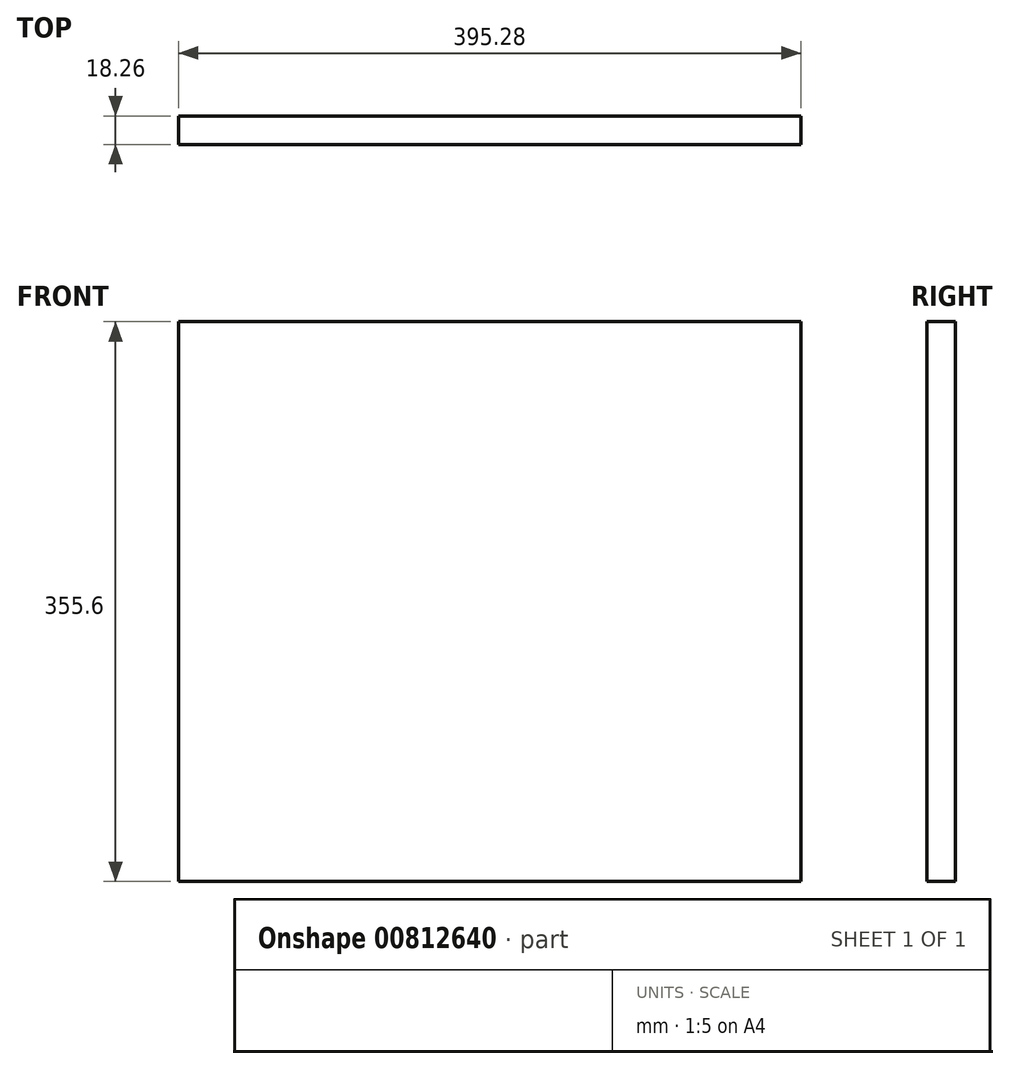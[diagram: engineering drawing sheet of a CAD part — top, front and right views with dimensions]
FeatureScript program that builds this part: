
annotation { "Feature Type Name" : "Feature", "Feature Type Description" : "" }
export const myFeature = defineFeature(function(context is Context, id is Id, definition is map)
    precondition{}
    {
        {
            var Q0;
            Q0=qCreatedBy(makeId("Front.planeOp"),FACE);
            var sketch = newSketch(context, id + "F0", { "sketchPlane" : qUnion([Q0])});
            skLineSegment(sketch, "E0.bottom", {"start": v(197.64, 177.8) * mm, "end": v(-197.64, 177.8) * mm});
            skLineSegment(sketch, "E0.top", {"start": v(197.64, -177.8) * mm, "end": v(-197.64, -177.8) * mm});
            skLineSegment(sketch, "E0.left", {"start": v(197.64, 177.8) * mm, "end": v(197.64, -177.8) * mm});
            skLineSegment(sketch, "E0.right", {"start": v(-197.64, 177.8) * mm, "end": v(-197.64, -177.8) * mm});
            skPoint(sketch, "E0.middle", {"position": v(0, 0) * mm});
            skSolve(sketch);
        }
        {
            var Q0;
            Q0=qSketchRegion(id+"F0",true);
            extrude(context, id + "F1", {"entities" : qUnion([Q0]), "depth" : 18.26 * mm, "offsetDistance" : 25.4 * mm});
        }
    });
